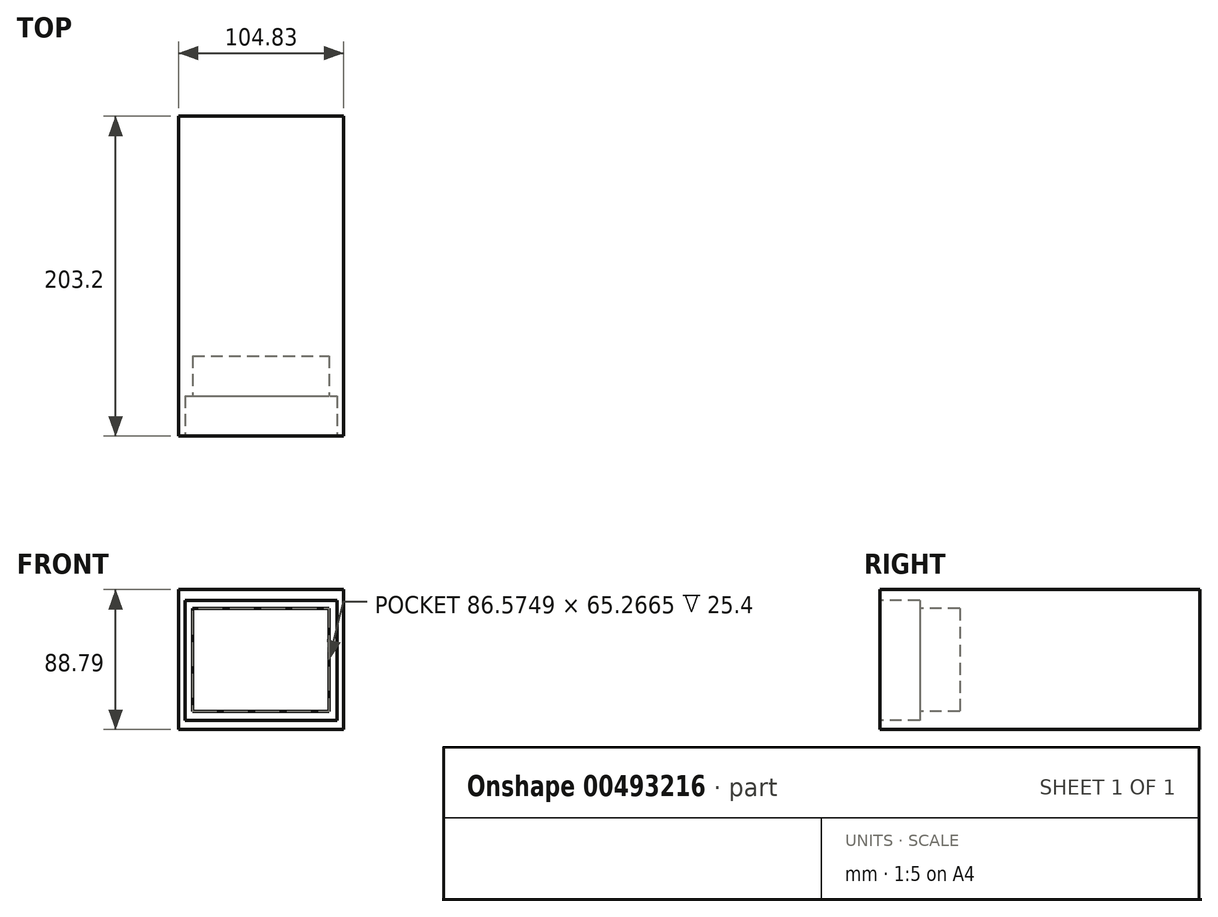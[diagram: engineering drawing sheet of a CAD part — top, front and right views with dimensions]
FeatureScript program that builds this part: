
annotation { "Feature Type Name" : "Feature", "Feature Type Description" : "" }
export const myFeature = defineFeature(function(context is Context, id is Id, definition is map)
    precondition{}
    {
        {
            var Q0;
            Q0=qCreatedBy(makeId("Front.planeOp"),FACE);
            var sketch = newSketch(context, id + "F0", { "sketchPlane" : qUnion([Q0])});
            skLineSegment(sketch, "E0.bottom", {"start": v(-50.8, 42.58) * mm, "end": v(54.04, 42.58) * mm});
            skLineSegment(sketch, "E0.top", {"start": v(-50.8, -46.21) * mm, "end": v(54.04, -46.21) * mm});
            skLineSegment(sketch, "E0.left", {"start": v(-50.8, 42.58) * mm, "end": v(-50.8, -46.21) * mm});
            skLineSegment(sketch, "E0.right", {"start": v(54.04, 42.58) * mm, "end": v(54.04, -46.21) * mm});
            skSolve(sketch);
        }
        {
            var Q0;
            Q0=makeQuery(id+"F0.imprint","IMPRINT",FACE,{"disambiguationData":[TD([[makeQuery(id+"F0.imprint","IMPRINT",EDGE,{"derivedFrom":sQuery(id+"F0.wireOp",EDGE,"E0.bottom")}),-1.0]])]});
            extrude(context, id + "F1", {"entities" : qUnion([Q0]), "depth" : 203.2 * mm});
        }
        {
            var Q0;
            Q0=makeQuery(id+"F1.opExtrude","CAP_FACE",FACE,{"disambiguationData":[OSD([sQuery(id+"F0.wireOp",EDGE,"E0.bottom"),sQuery(id+"F0.wireOp",EDGE,"E0.top"),sQuery(id+"F0.wireOp",EDGE,"E0.left"),sQuery(id+"F0.wireOp",EDGE,"E0.right")])],"isStart":false});
            var sketch = newSketch(context, id + "F2", { "sketchPlane" : qUnion([Q0])});
            skLineSegment(sketch, "E1.bottom", {"start": v(-46.6, 35.7) * mm, "end": v(49.84, 35.7) * mm});
            skLineSegment(sketch, "E1.top", {"start": v(-46.6, -40.48) * mm, "end": v(49.84, -40.48) * mm});
            skLineSegment(sketch, "E1.left", {"start": v(-46.6, 35.7) * mm, "end": v(-46.6, -40.48) * mm});
            skLineSegment(sketch, "E1.right", {"start": v(49.84, 35.7) * mm, "end": v(49.84, -40.48) * mm});
            skSolve(sketch);
        }
        {
            var Q0;
            Q0=makeQuery(id+"F2.imprint","IMPRINT",FACE,{"disambiguationData":[TD([[makeQuery(id+"F2.imprint","IMPRINT",EDGE,{"derivedFrom":sQuery(id+"F2.wireOp",EDGE,"E1.bottom")}),-1.0]])]});
            extrude(context, id + "F3", {"entities" : qUnion([Q0]), "operationType" : NewBodyOperationType.REMOVE, "oppositeDirection" : true, "depth" : 25.4 * mm});
        }
        {
            var Q0;
            Q0=makeQuery(id+"F3.boolean.opBoolean","COPY",FACE,{"derivedFrom":makeQuery(id+"F3.opExtrude","CAP_FACE",FACE,{"disambiguationData":[OSD([sQuery(id+"F2.wireOp",EDGE,"E1.bottom"),sQuery(id+"F2.wireOp",EDGE,"E1.top"),sQuery(id+"F2.wireOp",EDGE,"E1.left"),sQuery(id+"F2.wireOp",EDGE,"E1.right")])],"isStart":false})});
            var sketch = newSketch(context, id + "F4", { "sketchPlane" : qUnion([Q0])});
            skLineSegment(sketch, "E2.bottom", {"start": v(-41.72, 30.5) * mm, "end": v(44.85, 30.5) * mm});
            skLineSegment(sketch, "E2.top", {"start": v(-41.72, -34.76) * mm, "end": v(44.85, -34.76) * mm});
            skLineSegment(sketch, "E2.left", {"start": v(-41.72, 30.5) * mm, "end": v(-41.72, -34.76) * mm});
            skLineSegment(sketch, "E2.right", {"start": v(44.85, 30.5) * mm, "end": v(44.85, -34.76) * mm});
            skSolve(sketch);
        }
        {
            var Q0;
            Q0=makeQuery(id+"F4.imprint","IMPRINT",FACE,{"disambiguationData":[TD([[makeQuery(id+"F4.imprint","IMPRINT",EDGE,{"derivedFrom":sQuery(id+"F4.wireOp",EDGE,"E2.bottom")}),-1.0]])]});
            extrude(context, id + "F5", {"entities" : qUnion([Q0]), "operationType" : NewBodyOperationType.REMOVE, "oppositeDirection" : true, "depth" : 25.4 * mm});
        }
    });
